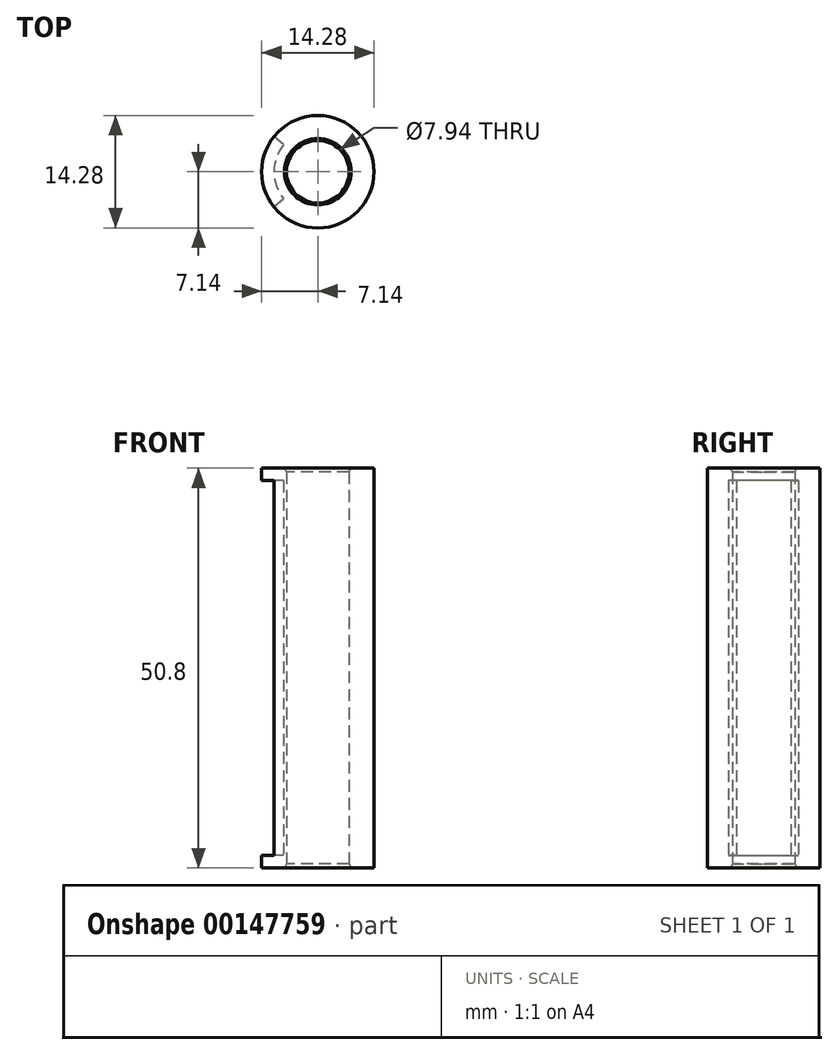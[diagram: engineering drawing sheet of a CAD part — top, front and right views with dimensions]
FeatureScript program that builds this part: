
annotation { "Feature Type Name" : "Feature", "Feature Type Description" : "" }
export const myFeature = defineFeature(function(context is Context, id is Id, definition is map)
    precondition{}
    {
        {
            var Q0;
            Q0=qCreatedBy(makeId("Top.planeOp"),FACE);
            var sketch = newSketch(context, id + "F0", { "sketchPlane" : qUnion([Q0])});
            skCircle(sketch, "E0", {"center": v(0, 0) * mm, "radius": 3.97 * mm});
            skCircle(sketch, "E1", {"center": v(0, 0) * mm, "radius": 7.14 * mm});
            skSolve(sketch);
        }
        {
            var Q0;
            Q0=makeQuery(id+"F0.imprint","IMPRINT",FACE,{"disambiguationData":[TD([[makeQuery(id+"F0.imprint","IMPRINT",EDGE,{"derivedFrom":sQuery(id+"F0.wireOp",EDGE,"E0")}),-1.0]])]});
            extrude(context, id + "F1", {"entities" : qUnion([Q0]), "depth" : 50.8 * mm});
        }
        {
            var Q0;
            Q0=makeQuery(id+"F1.opExtrude","CAP_EDGE",EDGE,{"disambiguationData":[OSD([sQuery(id+"F0.wireOp",EDGE,"E0")])],"isStart":false});
            var Q1;
            Q1=makeQuery(id+"F1.opExtrude","CAP_EDGE",EDGE,{"disambiguationData":[OSD([sQuery(id+"F0.wireOp",EDGE,"E0")])],"isStart":true});
            chamfer(context, id + "F2", {"entities" : qUnion([Q0, Q1]), "chamferType" : ChamferType.TWO_OFFSETS, "width1" : 0.5 * mm, "oppositeDirection" : false, "width2" : 0.25 * mm, "tangentPropagation" : true});
        }
        {
            var Q0;
            Q0=makeQuery(id+"F1.opExtrude","CAP_FACE",FACE,{"disambiguationData":[OSD([sQuery(id+"F0.wireOp",EDGE,"E0"),sQuery(id+"F0.wireOp",EDGE,"E1")])],"isStart":true});
            cPlane(context, id + "F3", {"entities" : qUnion([Q0]), "cplaneType" : CPlaneType.OFFSET, "offset" : 1.59 * mm, "oppositeDirection" : true, "width" : 152.4 * mm, "height" : 152.4 * mm});
        }
        {
            var Q0;
            Q0=qCreatedBy(id+"F3.planeOp",FACE);
            var sketch = newSketch(context, id + "F4", { "sketchPlane" : qUnion([Q0])});
            skArc(sketch, "E2", {"start": v(-4.34, 3.47) * mm, "mid": v(-5.56, 0) * mm, "end": v(-4.34, -3.47) * mm});
            skLineSegment(sketch, "E3", {"start": v(0, 0) * mm, "end": v(-4.34, -3.47) * mm, "construction": true});
            skLineSegment(sketch, "E4", {"start": v(0, 0) * mm, "end": v(-4.34, 3.47) * mm, "construction": true});
            skLineSegment(sketch, "E5", {"start": v(0, 0) * mm, "end": v(-5.56, 0) * mm, "construction": true});
            skLineSegment(sketch, "E6", {"start": v(-4.34, -3.47) * mm, "end": v(-5.58, -4.46) * mm});
            skLineSegment(sketch, "E7", {"start": v(-4.34, 3.47) * mm, "end": v(-5.58, 4.46) * mm});
            skArc(sketch, "E8", {"start": v(-5.58, 4.46) * mm, "mid": v(-7.14, 0) * mm, "end": v(-5.58, -4.46) * mm});
            skLineSegment(sketch, "E9", {"start": v(-5.58, 4.46) * mm, "end": v(-5.05, 5.05) * mm, "construction": true});
            skLineSegment(sketch, "E10", {"start": v(0, 0) * mm, "end": v(-5.05, 5.05) * mm, "construction": true});
            skLineSegment(sketch, "E11", {"start": v(0, 0) * mm, "end": v(-5.05, -5.05) * mm, "construction": true});
            skLineSegment(sketch, "E12", {"start": v(-5.58, -4.46) * mm, "end": v(-5.05, -5.05) * mm, "construction": true});
            skSolve(sketch);
        }
        {
            var Q0;
            Q0=makeQuery(id+"F1.opExtrude","CAP_FACE",FACE,{"disambiguationData":[OSD([sQuery(id+"F0.wireOp",EDGE,"E0"),sQuery(id+"F0.wireOp",EDGE,"E1")])],"isStart":false});
            cPlane(context, id + "F5", {"entities" : qUnion([Q0]), "cplaneType" : CPlaneType.OFFSET, "offset" : 1.59 * mm, "oppositeDirection" : true, "width" : 152.4 * mm, "height" : 152.4 * mm});
        }
        {
            var Q0;
            Q0=qSketchRegion(id+"F4",true);
            var Q1;
            Q1=qCreatedBy(id+"F5.planeOp",FACE);
            extrude(context, id + "F6", {"entities" : qUnion([Q0]), "operationType" : NewBodyOperationType.REMOVE, "endBound" : BoundingType.UP_TO_SURFACE, "oppositeDirection" : true, "endBoundEntityFace" : qUnion([Q1]), "depth" : 25.4 * mm});
        }
    });
